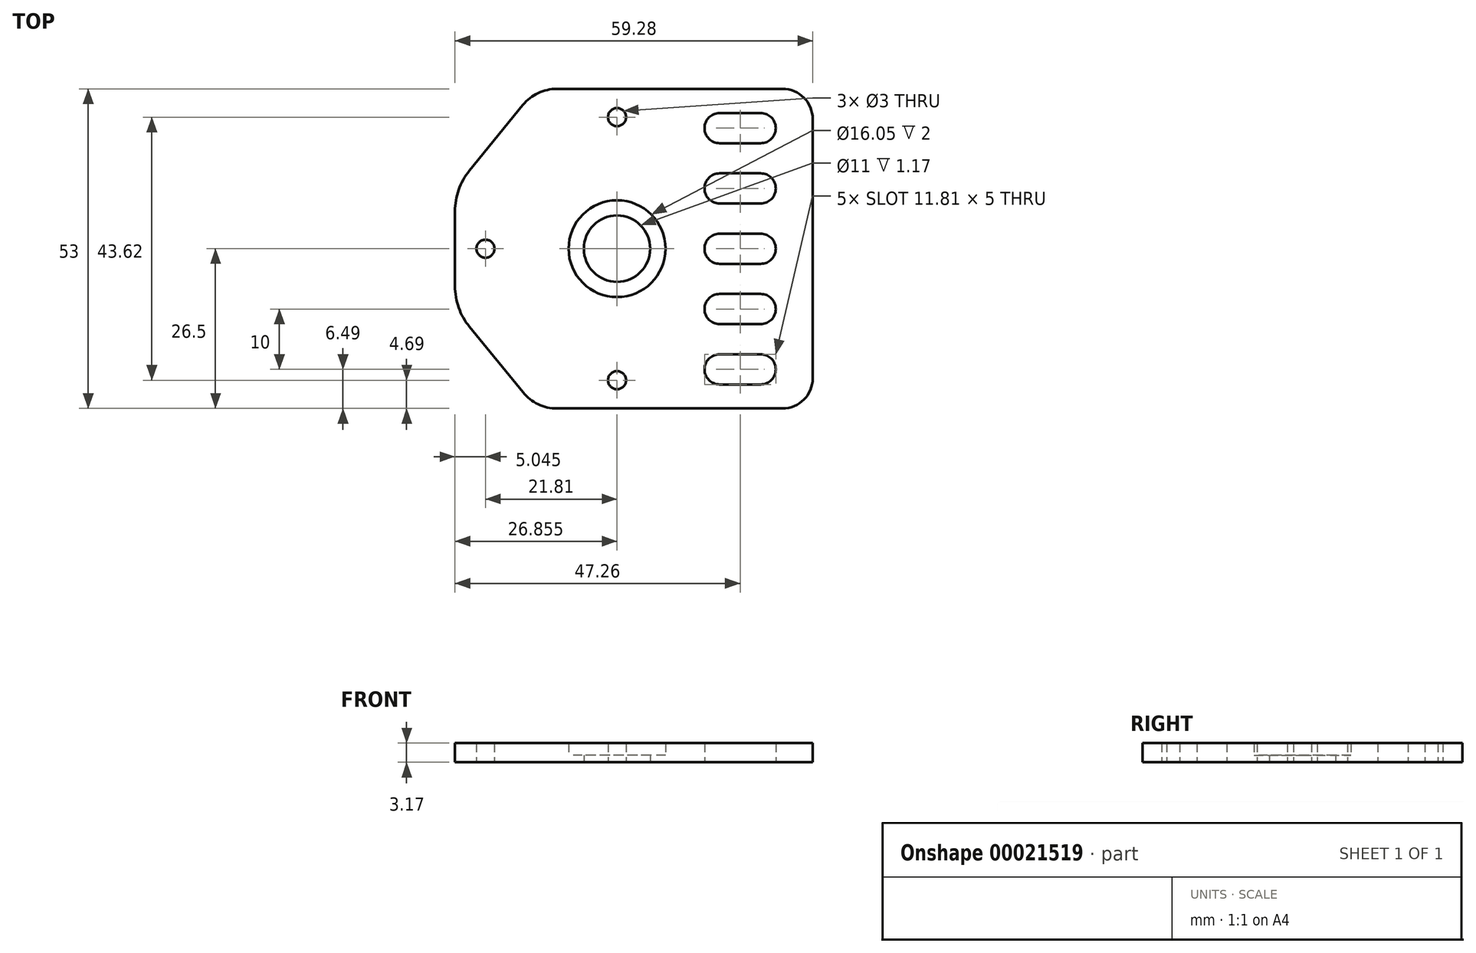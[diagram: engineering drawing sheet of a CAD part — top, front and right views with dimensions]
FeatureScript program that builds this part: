
annotation { "Feature Type Name" : "Feature", "Feature Type Description" : "" }
export const myFeature = defineFeature(function(context is Context, id is Id, definition is map)
    precondition{}
    {
        {
            var Q0;
            Q0=qCreatedBy(makeId("Top.planeOp"),FACE);
            var sketch = newSketch(context, id + "F0", { "sketchPlane" : qUnion([Q0])});
            skLineSegment(sketch, "E0.rect.bottom", {"start": v(24.64, 26.5) * mm, "end": v(-12.77, 26.5) * mm});
            skLineSegment(sketch, "E0.rect.top", {"start": v(24.64, -26.5) * mm, "end": v(-12.75, -26.5) * mm});
            skLineSegment(sketch, "E0.rect.left", {"start": v(29.65, 21.5) * mm, "end": v(29.64, -21.5) * mm});
            skLineSegment(sketch, "E0.rect.right", {"start": v(-29.64, 6.2) * mm, "end": v(-29.64, -6.2) * mm});
            skPoint(sketch, "E0.rect.middle", {"position": v(0, 0) * mm});
            skPoint(sketch, "E1.visualSharp", {"position": v(29.65, 26.5) * mm});
            skArc(sketch, "E1.filletArc", {"start": v(29.64, 21.5) * mm, "mid": v(28.18, 25.04) * mm, "end": v(24.64, 26.5) * mm});
            skPoint(sketch, "E2.visualSharp", {"position": v(29.64, -26.5) * mm});
            skArc(sketch, "E2.filletArc", {"start": v(24.64, -26.5) * mm, "mid": v(28.18, -25.04) * mm, "end": v(29.64, -21.5) * mm});
            skCircle(sketch, "E3", {"center": v(-2.79, 0) * mm, "radius": 5.5 * mm});
            skCircle(sketch, "E4", {"center": v(-2.79, 0) * mm, "radius": 8.03 * mm});
            skCircle(sketch, "E5", {"center": v(-2.79, 0) * mm, "radius": 10.5 * mm});
            skCircle(sketch, "E6", {"center": v(-2.79, -21.8) * mm, "radius": 1.5 * mm});
            skCircle(sketch, "E7.1.0", {"center": v(-24.6, 0) * mm, "radius": 1.5 * mm});
            skCircle(sketch, "E7.2.0", {"center": v(-2.79, 21.8) * mm, "radius": 1.5 * mm});
            skLineSegment(sketch, "E7.anchor1", {"start": v(-2.79, 0) * mm, "end": v(-2.79, -21.8) * mm, "construction": true});
            skLineSegment(sketch, "E7.anchor2", {"start": v(-2.79, 0) * mm, "end": v(-2.79, 21.8) * mm, "construction": true});
            skArc(sketch, "E8", {"start": v(14.22, -17.51) * mm, "mid": v(11.72, -20) * mm, "end": v(14.21, -22.5) * mm});
            skArc(sketch, "E9", {"start": v(21.03, -22.5) * mm, "mid": v(23.52, -20) * mm, "end": v(21.03, -17.51) * mm});
            skLineSegment(sketch, "E10", {"start": v(14.22, -17.51) * mm, "end": v(21.03, -17.51) * mm});
            skLineSegment(sketch, "E11", {"start": v(14.21, -22.5) * mm, "end": v(21.03, -22.5) * mm});
            skArc(sketch, "E12.0.1.0", {"start": v(14.22, -7.51) * mm, "mid": v(11.72, -10.01) * mm, "end": v(14.22, -12.5) * mm});
            skLineSegment(sketch, "E12.0.1.1", {"start": v(14.22, -12.5) * mm, "end": v(21.03, -12.5) * mm});
            skLineSegment(sketch, "E12.0.1.2", {"start": v(14.22, -7.51) * mm, "end": v(21.03, -7.51) * mm});
            skArc(sketch, "E12.0.1.3", {"start": v(21.03, -12.5) * mm, "mid": v(23.52, -10) * mm, "end": v(21.03, -7.51) * mm});
            skArc(sketch, "E12.0.2.0", {"start": v(14.21, 2.49) * mm, "mid": v(11.72, 0) * mm, "end": v(14.21, -2.5) * mm});
            skLineSegment(sketch, "E12.0.2.1", {"start": v(14.21, -2.5) * mm, "end": v(21.03, -2.5) * mm});
            skLineSegment(sketch, "E12.0.2.2", {"start": v(14.22, 2.49) * mm, "end": v(21.03, 2.49) * mm});
            skArc(sketch, "E12.0.2.3", {"start": v(21.03, -2.5) * mm, "mid": v(23.52, 0) * mm, "end": v(21.03, 2.49) * mm});
            skArc(sketch, "E12.0.3.0", {"start": v(14.21, 12.49) * mm, "mid": v(11.72, 10) * mm, "end": v(14.21, 7.5) * mm});
            skLineSegment(sketch, "E12.0.3.1", {"start": v(14.21, 7.5) * mm, "end": v(21.02, 7.5) * mm});
            skLineSegment(sketch, "E12.0.3.2", {"start": v(14.21, 12.49) * mm, "end": v(21.02, 12.49) * mm});
            skArc(sketch, "E12.0.3.3", {"start": v(21.02, 7.5) * mm, "mid": v(23.52, 10) * mm, "end": v(21.02, 12.49) * mm});
            skArc(sketch, "E12.0.4.0", {"start": v(14.21, 22.49) * mm, "mid": v(11.72, 20) * mm, "end": v(14.21, 17.5) * mm});
            skLineSegment(sketch, "E12.0.4.1", {"start": v(14.21, 17.5) * mm, "end": v(21.02, 17.5) * mm});
            skLineSegment(sketch, "E12.0.4.2", {"start": v(14.21, 22.49) * mm, "end": v(21.02, 22.49) * mm});
            skArc(sketch, "E12.0.4.3", {"start": v(21.02, 17.5) * mm, "mid": v(23.52, 20) * mm, "end": v(21.02, 22.49) * mm});
            skLineSegment(sketch, "E12.direction1", {"start": v(14.21, -22.5) * mm, "end": v(39.22, -22.5) * mm, "construction": true});
            skLineSegment(sketch, "E12.direction2", {"start": v(14.22, -22.5) * mm, "end": v(14.22, -12.5) * mm, "construction": true});
            skLineSegment(sketch, "E13", {"start": v(-27.25, 12.93) * mm, "end": v(-18.4, 23.83) * mm});
            skLineSegment(sketch, "E14", {"start": v(-27.24, -12.96) * mm, "end": v(-18.37, -23.83) * mm});
            skPoint(sketch, "E15.orphan", {"position": v(-29.64, 26.5) * mm});
            skPoint(sketch, "E16.orphan", {"position": v(-29.65, -26.5) * mm});
            skPoint(sketch, "E17.visualSharp", {"position": v(-16.22, 26.5) * mm});
            skArc(sketch, "E17.filletArc", {"start": v(-12.77, 26.5) * mm, "mid": v(-15.88, 25.8) * mm, "end": v(-18.4, 23.83) * mm});
            skPoint(sketch, "E18.visualSharp", {"position": v(-16.2, -26.5) * mm});
            skArc(sketch, "E18.filletArc", {"start": v(-18.37, -23.83) * mm, "mid": v(-15.86, -25.8) * mm, "end": v(-12.75, -26.5) * mm});
            skPoint(sketch, "E19.visualSharp", {"position": v(-29.64, 10) * mm});
            skArc(sketch, "E19.filletArc", {"start": v(-27.25, 12.93) * mm, "mid": v(-29.03, 9.77) * mm, "end": v(-29.65, 6.2) * mm});
            skPoint(sketch, "E20.visualSharp", {"position": v(-29.64, -10.01) * mm});
            skArc(sketch, "E20.filletArc", {"start": v(-29.65, -6.2) * mm, "mid": v(-29.03, -9.79) * mm, "end": v(-27.24, -12.96) * mm});
            skSolve(sketch);
        }
        {
            var Q0;
            Q0=makeQuery(id+"F0.imprint","IMPRINT",FACE,{"disambiguationData":[TD([[makeQuery(id+"F0.imprint","IMPRINT",EDGE,{"derivedFrom":sQuery(id+"F0.wireOp",EDGE,"E0.rect.bottom")}),1.0]])]});
            var Q1;
            Q1=makeQuery(id+"F0.imprint","IMPRINT",FACE,{"disambiguationData":[TD([[makeQuery(id+"F0.imprint","IMPRINT",EDGE,{"derivedFrom":sQuery(id+"F0.wireOp",EDGE,"E4")}),-1.0]])]});
            extrude(context, id + "F1", {"entities" : qUnion([Q0, Q1]), "depth" : 3.17 * mm});
        }
        {
            var Q0;
            Q0=makeQuery(id+"F0.imprint","IMPRINT",FACE,{"disambiguationData":[TD([[makeQuery(id+"F0.imprint","IMPRINT",EDGE,{"derivedFrom":sQuery(id+"F0.wireOp",EDGE,"E3")}),-1.0]])]});
            extrude(context, id + "F2", {"entities" : qUnion([Q0]), "operationType" : NewBodyOperationType.ADD, "depth" : 1.17 * mm});
        }
    });
